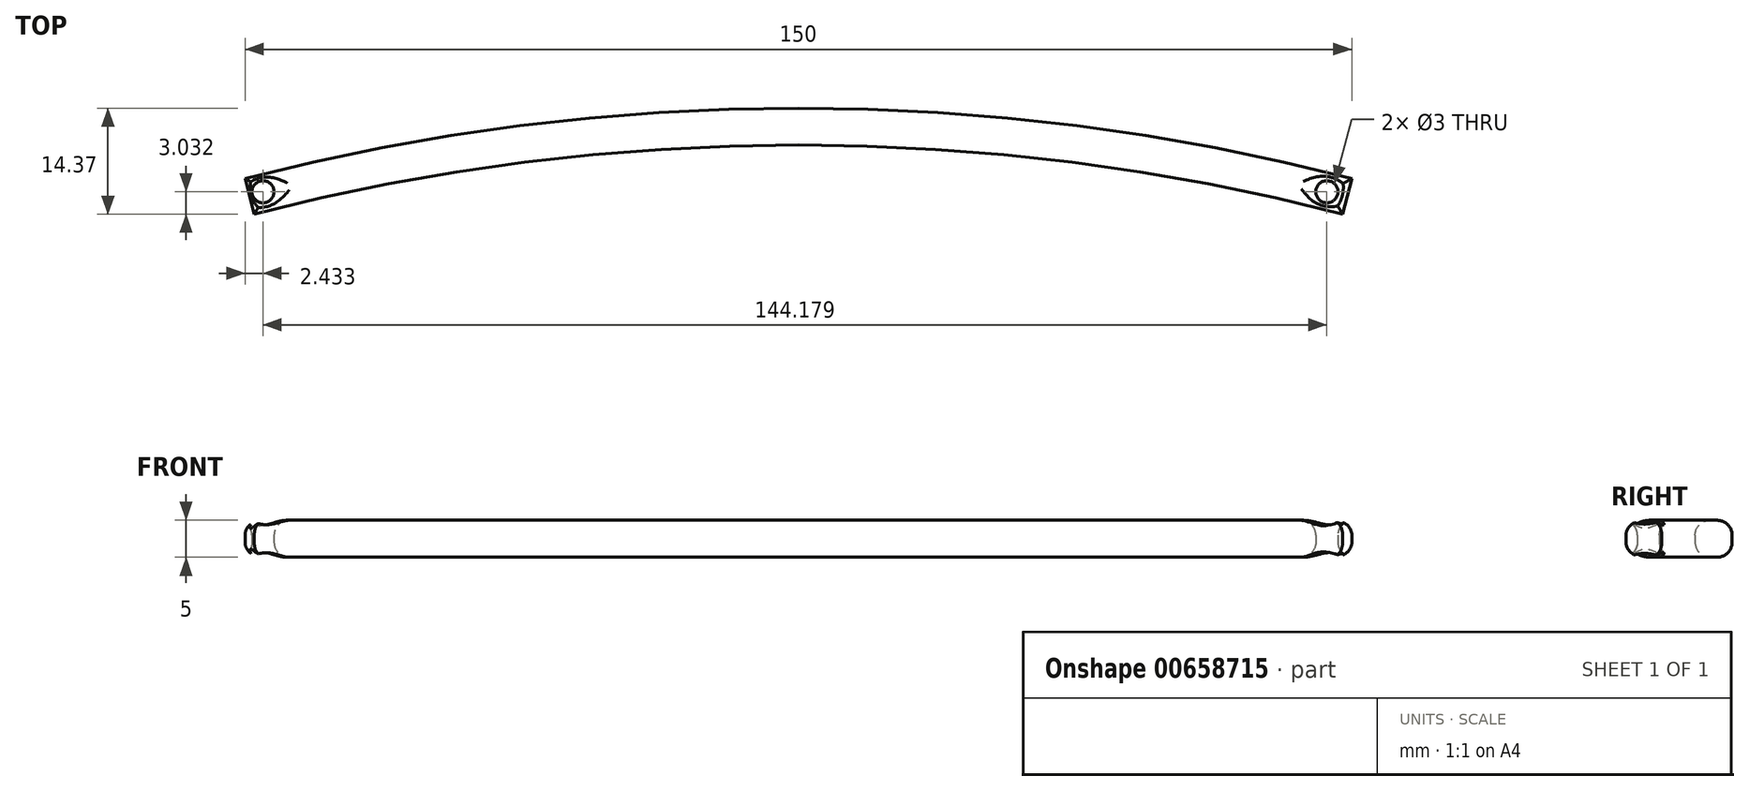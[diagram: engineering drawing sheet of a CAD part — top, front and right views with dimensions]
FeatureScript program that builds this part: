
annotation { "Feature Type Name" : "Feature", "Feature Type Description" : "" }
export const myFeature = defineFeature(function(context is Context, id is Id, definition is map)
    precondition{}
    {
        {
            var Q0;
            Q0=qCreatedBy(makeId("Top.planeOp"),FACE);
            var sketch = newSketch(context, id + "F0", { "sketchPlane" : qUnion([Q0])});
            skArc(sketch, "E0", {"start": v(75, 0) * mm, "mid": v(0, 9.53) * mm, "end": v(-75, 0) * mm});
            skLineSegment(sketch, "E1", {"start": v(-75, 0) * mm, "end": v(0, 0) * mm, "construction": true});
            skLineSegment(sketch, "E2", {"start": v(75, 0) * mm, "end": v(0, 0) * mm, "construction": true});
            skArc(sketch, "E3.0", {"start": v(73.75, -4.84) * mm, "mid": v(0, 4.53) * mm, "end": v(-73.75, -4.84) * mm});
            skLineSegment(sketch, "E4", {"start": v(-75, 0) * mm, "end": v(-73.75, -4.84) * mm});
            skLineSegment(sketch, "E5", {"start": v(75, 0) * mm, "end": v(73.75, -4.84) * mm});
            skCircle(sketch, "E6", {"center": v(-72.57, -1.8) * mm, "radius": 1.5 * mm});
            skCircle(sketch, "E7", {"center": v(71.61, -1.8) * mm, "radius": 1.5 * mm});
            skSolve(sketch);
        }
        {
            var Q0;
            Q0=makeQuery(id+"F0.imprint","IMPRINT",FACE,{"disambiguationData":[TD([[makeQuery(id+"F0.imprint","IMPRINT",EDGE,{"derivedFrom":sQuery(id+"F0.wireOp",EDGE,"E0")}),1.0]])]});
            extrude(context, id + "F1", {"entities" : qUnion([Q0]), "depth" : 5 * mm, "offsetDistance" : 25 * mm});
        }
        {
            var Q0;
            Q0=makeQuery(id+"F1.opExtrude","CAP_FACE",FACE,{"disambiguationData":[OSD([sQuery(id+"F0.wireOp",EDGE,"E0"),sQuery(id+"F0.wireOp",EDGE,"E3.0"),sQuery(id+"F0.wireOp",EDGE,"E4"),sQuery(id+"F0.wireOp",EDGE,"E5"),sQuery(id+"F0.wireOp",EDGE,"E6"),sQuery(id+"F0.wireOp",EDGE,"E7")])],"isStart":false});
            var Q1;
            Q1=makeQuery(id+"F1.opExtrude","CAP_FACE",FACE,{"disambiguationData":[OSD([sQuery(id+"F0.wireOp",EDGE,"E0"),sQuery(id+"F0.wireOp",EDGE,"E3.0"),sQuery(id+"F0.wireOp",EDGE,"E4"),sQuery(id+"F0.wireOp",EDGE,"E5"),sQuery(id+"F0.wireOp",EDGE,"E6"),sQuery(id+"F0.wireOp",EDGE,"E7")])],"isStart":true});
            fillet(context, id + "F2", {"entities" : qUnion([Q0, Q1]), "radius" : 2 * mm, "tangentPropagation" : true, "allowEdgeOverflow" : false});
        }
    });
